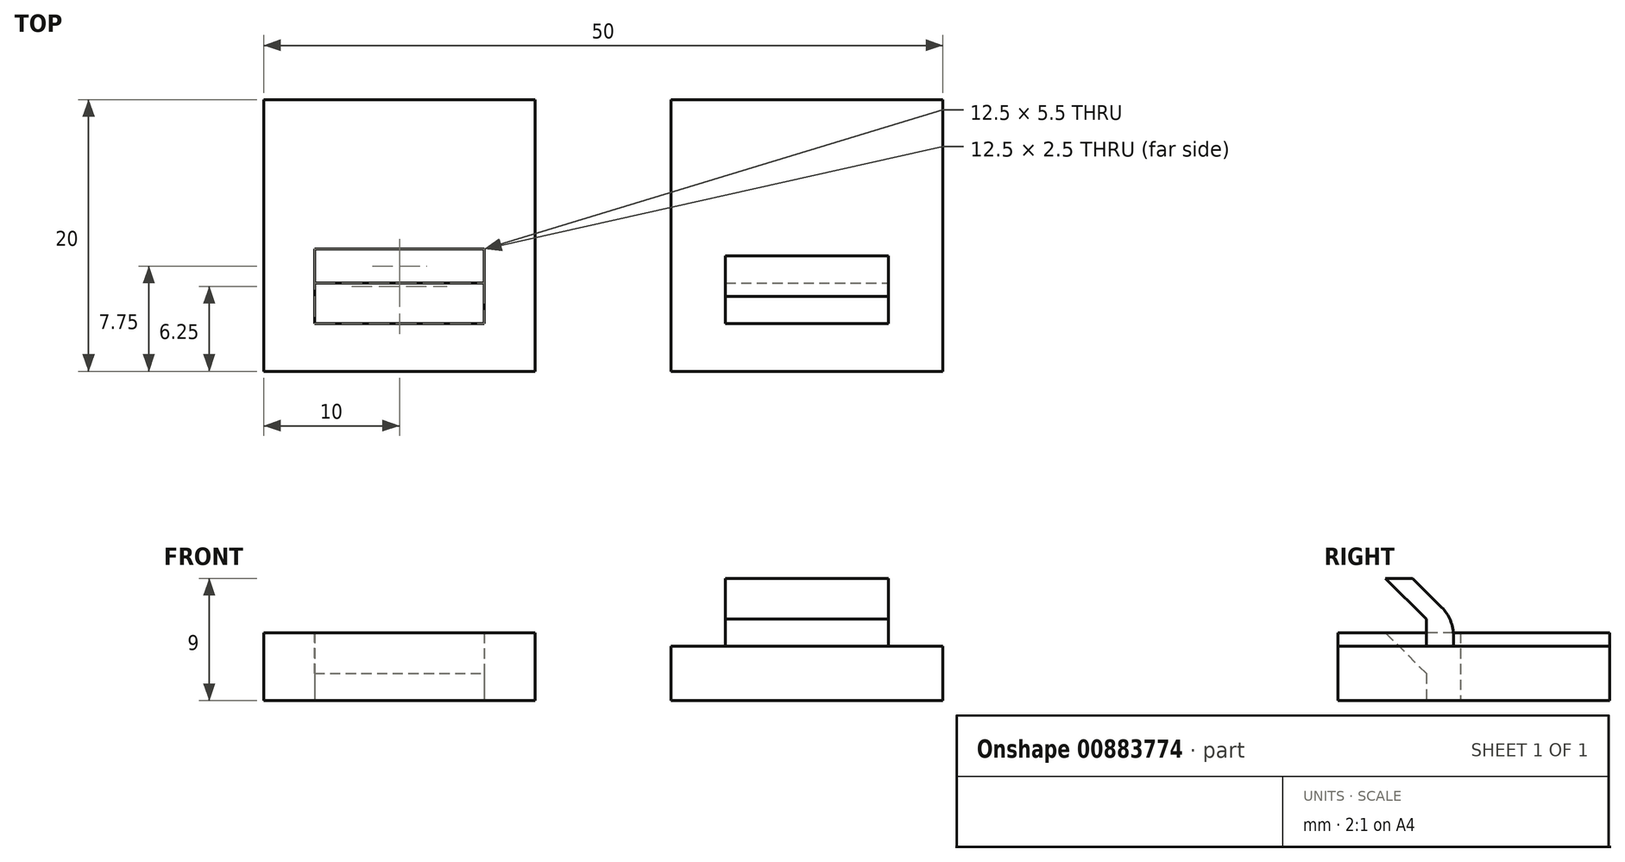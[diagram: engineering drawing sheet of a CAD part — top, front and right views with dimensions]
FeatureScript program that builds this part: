
annotation { "Feature Type Name" : "Feature", "Feature Type Description" : "" }
export const myFeature = defineFeature(function(context is Context, id is Id, definition is map)
    precondition{}
    {
        {
            var Q0;
            Q0=qCreatedBy(makeId("Top.planeOp"),FACE);
            var sketch = newSketch(context, id + "F0", { "sketchPlane" : qUnion([Q0])});
            skLineSegment(sketch, "E0.bottom", {"start": v(-25, 10) * mm, "end": v(-5, 10) * mm});
            skLineSegment(sketch, "E0.top", {"start": v(-25, -10) * mm, "end": v(-5, -10) * mm});
            skLineSegment(sketch, "E0.left", {"start": v(-25, 10) * mm, "end": v(-25, -10) * mm});
            skLineSegment(sketch, "E0.right", {"start": v(-5, 10) * mm, "end": v(-5, -10) * mm});
            skLineSegment(sketch, "E1.bottom", {"start": v(5, 10) * mm, "end": v(25, 10) * mm});
            skLineSegment(sketch, "E1.top", {"start": v(5, -10) * mm, "end": v(25, -10) * mm});
            skLineSegment(sketch, "E1.left", {"start": v(5, 10) * mm, "end": v(5, -10) * mm});
            skLineSegment(sketch, "E1.right", {"start": v(25, 10) * mm, "end": v(25, -10) * mm});
            skLineSegment(sketch, "E2.bottom", {"start": v(-21.25, -1) * mm, "end": v(-8.75, -1) * mm});
            skLineSegment(sketch, "E2.top", {"start": v(-21.25, -3.5) * mm, "end": v(-8.75, -3.5) * mm});
            skLineSegment(sketch, "E2.left", {"start": v(-21.25, -1) * mm, "end": v(-21.25, -3.5) * mm});
            skLineSegment(sketch, "E2.right", {"start": v(-8.75, -1) * mm, "end": v(-8.75, -3.5) * mm});
            skLineSegment(sketch, "E3", {"start": v(-15, 15.4) * mm, "end": v(-15, -14.78) * mm, "construction": true});
            skLineSegment(sketch, "E4", {"start": v(15, 14.68) * mm, "end": v(15, -14.78) * mm, "construction": true});
            skLineSegment(sketch, "E5.bottom", {"start": v(9, -1.5) * mm, "end": v(21, -1.5) * mm});
            skLineSegment(sketch, "E5.top", {"start": v(9, -6.5) * mm, "end": v(21, -6.5) * mm});
            skLineSegment(sketch, "E5.left", {"start": v(9, -1.5) * mm, "end": v(9, -6.5) * mm});
            skLineSegment(sketch, "E5.right", {"start": v(21, -1.5) * mm, "end": v(21, -6.5) * mm});
            skSolve(sketch);
        }
        {
            var Q0;
            Q0=makeQuery(id+"F0.imprint","IMPRINT",FACE,{"disambiguationData":[TD([[makeQuery(id+"F0.imprint","IMPRINT",EDGE,{"derivedFrom":sQuery(id+"F0.wireOp",EDGE,"E5.bottom")}),-1.0]])]});
            extrude(context, id + "F1", {"entities" : qUnion([Q0]), "depth" : 9 * mm, "offsetDistance" : 25 * mm});
        }
        {
            var Q0;
            Q0=makeQuery(id+"F0.imprint","IMPRINT",FACE,{"disambiguationData":[TD([[makeQuery(id+"F0.imprint","IMPRINT",EDGE,{"derivedFrom":sQuery(id+"F0.wireOp",EDGE,"E1.bottom")}),-1.0]])]});
            extrude(context, id + "F2", {"entities" : qUnion([Q0]), "operationType" : NewBodyOperationType.ADD, "depth" : 4 * mm, "offsetDistance" : 25 * mm});
        }
        {
            var Q0;
            Q0=makeQuery(id+"F0.imprint","IMPRINT",FACE,{"disambiguationData":[TD([[makeQuery(id+"F0.imprint","IMPRINT",EDGE,{"derivedFrom":sQuery(id+"F0.wireOp",EDGE,"E0.bottom")}),-1.0]])]});
            extrude(context, id + "F3", {"entities" : qUnion([Q0]), "depth" : 5 * mm, "offsetDistance" : 25 * mm});
        }
        {
            var Q0;
            Q0=makeQuery(id+"F3.opExtrude","CAP_EDGE",EDGE,{"disambiguationData":[OSD([sQuery(id+"F0.wireOp",EDGE,"E2.top")])],"isStart":false});
            chamfer(context, id + "F4", {"entities" : qUnion([Q0]), "chamferType" : ChamferType.OFFSET_ANGLE, "width" : 3 * mm, "oppositeDirection" : false, "angle" : 45 * degree, "tangentPropagation" : true});
        }
        {
            var Q0;
            Q0=makeQuery(id+"F1.opExtrude","SWEPT_FACE",FACE,{"disambiguationData":[OSD([sQuery(id+"F0.wireOp",EDGE,"E5.right")])]});
            var sketch = newSketch(context, id + "F5", { "sketchPlane" : qUnion([Q0])});
            skLineSegment(sketch, "E6", {"start": v(-6.5, 9) * mm, "end": v(-3.5, 6) * mm});
            skLineSegment(sketch, "E7", {"start": v(-3.5, 6) * mm, "end": v(-3.5, 4) * mm});
            skSolve(sketch);
        }
        {
            var Q0;
            Q0=makeQuery(id+"F5.imprint","IMPRINT",FACE,{"disambiguationData":[TD([[makeQuery(id+"F5.imprint","IMPRINT",EDGE,{"derivedFrom":sQuery(id+"F5.wireOp",EDGE,"E6")}),-1.0]])]});
            extrude(context, id + "F6", {"entities" : qUnion([Q0]), "operationType" : NewBodyOperationType.REMOVE, "oppositeDirection" : true, "depth" : 12 * mm, "offsetDistance" : 25 * mm});
        }
        {
            var Q0;
            Q0=makeQuery(id+"F1.opExtrude","CAP_EDGE",EDGE,{"disambiguationData":[OSD([sQuery(id+"F0.wireOp",EDGE,"E5.bottom")])],"isStart":false});
            chamfer(context, id + "F7", {"entities" : qUnion([Q0]), "width" : 3 * mm, "tangentPropagation" : true});
        }
        {
            var Q0;
            {var subQ0=sQuery(id+"F0.wireOp",EDGE,"E5.bottom");Q0=makeQuery(id+"F7.opChamfer","BLEND_EDGE",EDGE,{"blendedFrom":[makeQuery(id+"F1.opExtrude","CAP_EDGE",EDGE,{"disambiguationData":[OSD([subQ0])],"isStart":false}),makeQuery(id+"F1.opExtrude","SWEPT_FACE",FACE,{"disambiguationData":[OSD([subQ0])]})],"blendedInto":[makeQuery(id+"F1.opExtrude","SWEPT_FACE",FACE,{"disambiguationData":[OSD([subQ0])]})]});}
            fillet(context, id + "F8", {"entities" : qUnion([Q0]), "tangentPropagation" : true, "radius" : 3 * mm, "defaultsChanged" : true, "vertexSettings" : [], "allowEdgeOverflow" : false});
        }
    });
